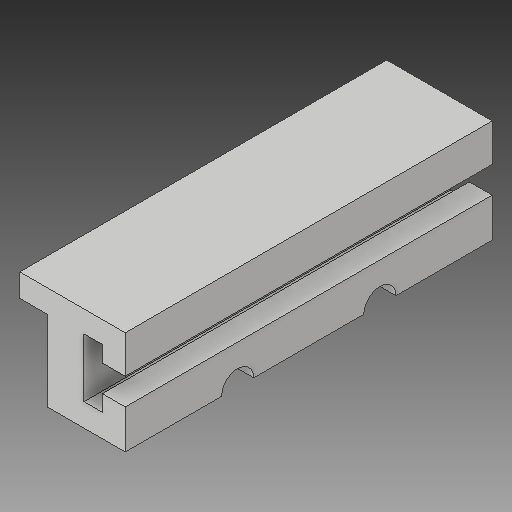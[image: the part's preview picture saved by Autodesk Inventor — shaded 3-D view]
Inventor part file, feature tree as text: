
AUTODESK INVENTOR PART (.ipt)
format: ipt  version: 2019 (Build 230136000, 136)  size: 131,072 bytes
history: native  units: mm
features: extrude x2, sketch x2, plane x1, mirror x1, projected_geometry x1
ambient origin geometry x8: Origin, YZ Plane, XZ Plane, XY Plane, X Axis, Y Axis, Z Axis, Center Point
bodies: Solid1 (feature_tree)
feature tree (7):
  extrude  "Extrusion1"  Depth=5.0mm
  extrude  "Extrusion2"  Depth=5.0mm
  plane  "Work Plane1"
  mirror  "Mirror1"
  sketch  "Sketch1"  dims[d0=6.0mm d1=5.0mm]
  sketch  "Sketch2"  dims[d4=4.0mm d8=5.0mm d10=5.8mm d12=3.5mm d13=3.5mm d15=80.0mm d16=0.0mm d17=0.3mm d18=17.0mm d19=8.0mm d20=0.0mm d21=7.0mm d22=7.0mm d24=24.5mm d25=20.0mm d26=0.0mm d27=40.0mm]
  projected_geometry  "Projected Loop1"
